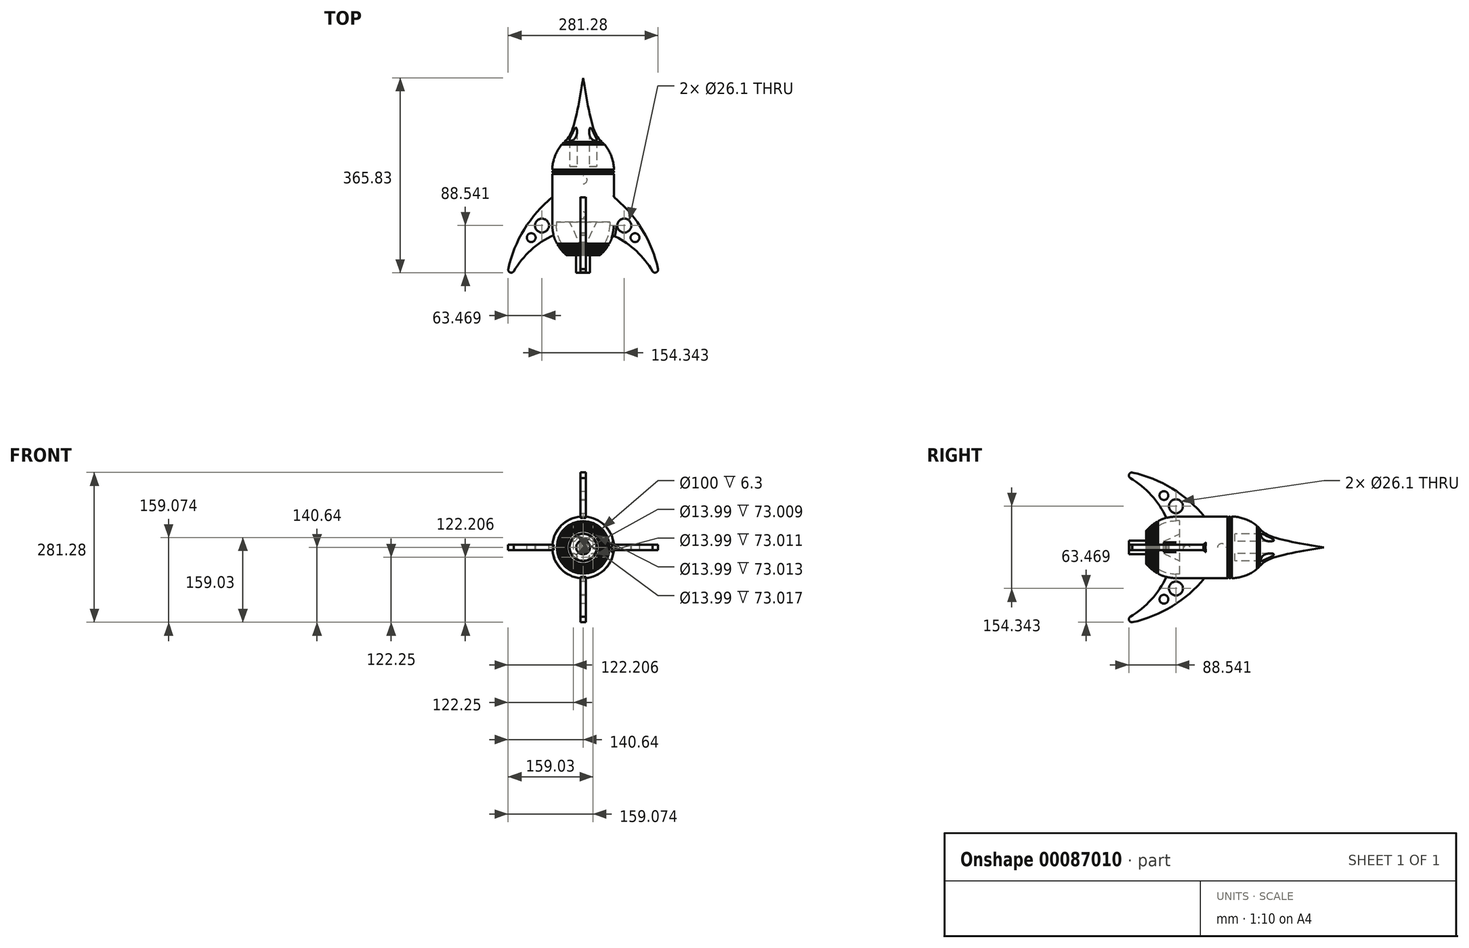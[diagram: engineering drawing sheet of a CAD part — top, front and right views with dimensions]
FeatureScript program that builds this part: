
annotation { "Feature Type Name" : "Feature", "Feature Type Description" : "" }
export const myFeature = defineFeature(function(context is Context, id is Id, definition is map)
    precondition{}
    {
        {
            var Q0;
            Q0=qCreatedBy(makeId("Right.planeOp"),FACE);
            var sketch = newSketch(context, id + "F0", { "sketchPlane" : qUnion([Q0])});
            skLineSegment(sketch, "E0", {"start": v(-55.59, 50) * mm, "end": v(46.96, 50) * mm});
            skArc(sketch, "E1", {"start": v(95.35, 30.1) * mm, "mid": v(73.12, 44.83) * mm, "end": v(46.96, 50) * mm});
            skArc(sketch, "E2", {"start": v(-55.59, 50) * mm, "mid": v(-83.4, 43.72) * mm, "end": v(-105.8, 26.08) * mm});
            skArc(sketch, "E3.0", {"start": v(-55.59, 57.95) * mm, "mid": v(-86.8, 50.89) * mm, "end": v(-111.96, 31.1) * mm});
            skLineSegment(sketch, "E3.1", {"start": v(-55.59, 57.95) * mm, "end": v(46.96, 57.95) * mm});
            skArc(sketch, "E3.2", {"start": v(99.6, 37.03) * mm, "mid": v(75.28, 52.53) * mm, "end": v(46.96, 57.95) * mm});
            skLineSegment(sketch, "E4", {"start": v(-111.96, 31.1) * mm, "end": v(-105.8, 26.08) * mm});
            skLineSegment(sketch, "E5", {"start": v(95.35, 30.1) * mm, "end": v(99.6, 37.03) * mm});
            skLineSegment(sketch, "E6", {"start": v(-312.53, 0) * mm, "end": v(235.17, 0) * mm, "construction": true});
            skLineSegment(sketch, "E7", {"start": v(-103.73, 0) * mm, "end": v(-49.29, 25.17) * mm});
            skLineSegment(sketch, "E8", {"start": v(-49.29, 25.17) * mm, "end": v(-49.29, 50) * mm});
            skLineSegment(sketch, "E9", {"start": v(-49.29, 50) * mm, "end": v(-42.87, 50) * mm});
            skLineSegment(sketch, "E10", {"start": v(-42.87, 50) * mm, "end": v(-42.87, 0) * mm});
            skLineSegment(sketch, "E11", {"start": v(-42.87, 0) * mm, "end": v(-103.73, 0) * mm});
            skFitSpline(sketch, "E12", {"points": [v(99.6, 37.03) * mm, v(116.25, 23.47) * mm, v(221.16, 0) * mm], "startDerivative": vector(38.76, -45.45) * mm, "endDerivative": vector(185.64, -30.52) * mm});
            skLineSegment(sketch, "E13", {"start": v(46.34, 0) * mm, "end": v(221.16, 0) * mm});
            skPoint(sketch, "E14", {"position": v(73.12, 44.83) * mm});
            skLineSegment(sketch, "E15", {"start": v(46.96, 50) * mm, "end": v(48.2, 0) * mm});
            skLineSegment(sketch, "E16", {"start": v(48.2, 0) * mm, "end": v(221.16, 0) * mm});
            skLineSegment(sketch, "E17.bottom", {"start": v(46.96, 50) * mm, "end": v(-42.87, 50) * mm});
            skLineSegment(sketch, "E17.top", {"start": v(46.96, 0) * mm, "end": v(-42.87, 0) * mm});
            skLineSegment(sketch, "E17.left", {"start": v(46.96, 50) * mm, "end": v(46.96, 0) * mm});
            skLineSegment(sketch, "E18", {"start": v(48.2, 0) * mm, "end": v(46.96, 0) * mm});
            skLineSegment(sketch, "E19.bottom", {"start": v(-100.59, 0) * mm, "end": v(-144.67, 0) * mm});
            skLineSegment(sketch, "E19.top", {"start": v(-100.59, 12.97) * mm, "end": v(-144.67, 12.97) * mm});
            skLineSegment(sketch, "E19.left", {"start": v(-100.59, 0) * mm, "end": v(-100.59, 12.97) * mm});
            skLineSegment(sketch, "E19.right", {"start": v(-144.67, 0) * mm, "end": v(-144.67, 12.97) * mm});
            skSolve(sketch);
        }
        {
            var Q0;
            Q0 = qSketchRegion(id + "F0", true);
            var Q1;
            Q1=sQuery(id+"F0.wireOp",EDGE,"E6");
            revolve(context, id + "F1", {"entities" : qUnion([Q0]), "axis" : qUnion([Q1]), "revolveType" : RevolveType.FULL});
        }
        {
            var Q0;
            Q0=qCreatedBy(makeId("Top.planeOp"),FACE);
            var sketch = newSketch(context, id + "F2", { "sketchPlane" : qUnion([Q0])});
            skCircle(sketch, "E20", {"center": v(0, -35.48) * mm, "radius": 5 * mm});
            skCircle(sketch, "E21", {"center": v(0, 29.75) * mm, "radius": 7.5 * mm});
            skSolve(sketch);
        }
        {
            var Q0;
            Q0=makeQuery(id+"F2.imprint","IMPRINT",FACE,{"disambiguationData":[TD([[makeQuery(id+"F2.imprint","IMPRINT",EDGE,{"derivedFrom":sQuery(id+"F2.wireOp",EDGE,"E20")}),1.0]])]});
            extrude(context, id + "F3", {"entities" : qUnion([Q0]), "operationType" : NewBodyOperationType.REMOVE, "endBound" : BoundingType.SYMMETRIC, "depth" : 220.94 * mm});
        }
        {
            var Q0;
            Q0=makeQuery(id+"F2.imprint","IMPRINT",FACE,{"disambiguationData":[TD([[makeQuery(id+"F2.imprint","IMPRINT",EDGE,{"derivedFrom":sQuery(id+"F2.wireOp",EDGE,"E21")}),1.0]])]});
            extrude(context, id + "F4", {"entities" : qUnion([Q0]), "operationType" : NewBodyOperationType.REMOVE, "endBound" : BoundingType.SYMMETRIC, "depth" : 208.68 * mm});
        }
        {
            var Q0;
            Q0=qCreatedBy(makeId("Top.planeOp"),FACE);
            var sketch = newSketch(context, id + "F5", { "sketchPlane" : qUnion([Q0])});
            skArc(sketch, "E22", {"start": v(130.13, -141.96) * mm, "mid": v(97.17, -101.6) * mm, "end": v(53.5, -73.17) * mm});
            skArc(sketch, "E23", {"start": v(140.55, -137.77) * mm, "mid": v(109.33, -61.42) * mm, "end": v(54.26, 0) * mm});
            skLineSegment(sketch, "E24", {"start": v(53.5, -73.17) * mm, "end": v(54.26, 0) * mm});
            skArc(sketch, "E25", {"start": v(130.13, -141.96) * mm, "mid": v(137.28, -143.98) * mm, "end": v(140.44, -137.26) * mm});
            skCircle(sketch, "E26", {"center": v(77.17, -56.13) * mm, "radius": 13.05 * mm});
            skCircle(sketch, "E27", {"center": v(97.37, -78.71) * mm, "radius": 8.3 * mm});
            skSolve(sketch);
        }
        {
            var Q0;
            Q0=makeQuery(id+"F5.imprint","IMPRINT",FACE,{"disambiguationData":[TD([[makeQuery(id+"F5.imprint","IMPRINT",EDGE,{"derivedFrom":sQuery(id+"F5.wireOp",EDGE,"E22")}),-1.0]])]});
            extrude(context, id + "F6", {"entities" : qUnion([Q0]), "operationType" : NewBodyOperationType.ADD, "endBound" : BoundingType.SYMMETRIC, "depth" : 10 * mm});
        }
        {
            var Q0;
            Q0=makeQuery(id+"F1.opRevolve","SWEPT_BODY",BODY,{"disambiguationData":[OSD([sQuery(id+"F0.wireOp",EDGE,"E0"),sQuery(id+"F0.wireOp",EDGE,"E1"),sQuery(id+"F0.wireOp",EDGE,"E2"),sQuery(id+"F0.wireOp",EDGE,"E3.0"),sQuery(id+"F0.wireOp",EDGE,"E3.1"),sQuery(id+"F0.wireOp",EDGE,"E3.2"),sQuery(id+"F0.wireOp",EDGE,"E4"),sQuery(id+"F0.wireOp",EDGE,"E5")])]});
            var Q1;
            Q1=sQuery(id+"F0.wireOp",EDGE,"E6");
            circularPattern(context, id + "F7", {"operationType" : NewBodyOperationType.ADD, "entities" : qUnion([Q0]), "axis" : qUnion([Q1]), "angle" : 360 * degree, "instanceCount" : 4, "equalSpace" : true});
        }
        {
            var Q0;
            Q0=qCreatedBy(makeId("Front.planeOp"),FACE);
            var sketch = newSketch(context, id + "F8", { "sketchPlane" : qUnion([Q0])});
            skCircle(sketch, "E28", {"center": v(-18.4, -18.43) * mm, "radius": 7 * mm});
            skCircle(sketch, "E29.1.0", {"center": v(18.43, -18.4) * mm, "radius": 7 * mm});
            skCircle(sketch, "E29.2.0", {"center": v(18.4, 18.43) * mm, "radius": 7 * mm});
            skCircle(sketch, "E29.3.0", {"center": v(-18.43, 18.4) * mm, "radius": 7 * mm});
            skPoint(sketch, "E29.center", {"position": v(0, 0) * mm});
            skSolve(sketch);
        }
        {
            var Q0;
            Q0=makeQuery(id+"F8.imprint","IMPRINT",FACE,{"disambiguationData":[TD([[makeQuery(id+"F8.imprint","IMPRINT",EDGE,{"derivedFrom":sQuery(id+"F8.wireOp",EDGE,"E28")}),1.0]])]});
            var Q1;
            Q1=makeQuery(id+"F8.imprint","IMPRINT",FACE,{"disambiguationData":[TD([[makeQuery(id+"F8.imprint","IMPRINT",EDGE,{"derivedFrom":sQuery(id+"F8.wireOp",EDGE,"E29.3.0")}),1.0]])]});
            var Q2;
            Q2=makeQuery(id+"F8.imprint","IMPRINT",FACE,{"disambiguationData":[TD([[makeQuery(id+"F8.imprint","IMPRINT",EDGE,{"derivedFrom":sQuery(id+"F8.wireOp",EDGE,"E29.2.0")}),1.0]])]});
            var Q3;
            Q3=makeQuery(id+"F8.imprint","IMPRINT",FACE,{"disambiguationData":[TD([[makeQuery(id+"F8.imprint","IMPRINT",EDGE,{"derivedFrom":sQuery(id+"F8.wireOp",EDGE,"E29.1.0")}),1.0]])]});
            extrude(context, id + "F9", {"entities" : qUnion([Q0, Q1, Q2, Q3]), "oppositeDirection" : true, "depth" : 171.7 * mm, "hasSecondDirection" : true, "secondDirectionOppositeDirection" : true, "secondDirectionDepth" : 54.52 * mm});
        }
        {
            var Q0;
            Q0=makeQuery(id+"F9.opExtrude","SWEPT_BODY",BODY,{"disambiguationData":[OSD([sQuery(id+"F8.wireOp",EDGE,"E29.3.0")])]});
            var Q1;
            Q1=makeQuery(id+"F9.opExtrude","SWEPT_BODY",BODY,{"disambiguationData":[OSD([sQuery(id+"F8.wireOp",EDGE,"E29.2.0")])]});
            var Q2;
            Q2=makeQuery(id+"F9.opExtrude","SWEPT_BODY",BODY,{"disambiguationData":[OSD([sQuery(id+"F8.wireOp",EDGE,"E29.1.0")])]});
            var Q3;
            Q3=makeQuery(id+"F9.opExtrude","SWEPT_BODY",BODY,{"disambiguationData":[OSD([sQuery(id+"F8.wireOp",EDGE,"E28")])]});
            var Q4;
            Q4=makeQuery(id+"F1.opRevolve","SWEPT_BODY",BODY,{"disambiguationData":[OSD([sQuery(id+"F0.wireOp",EDGE,"E0"),sQuery(id+"F0.wireOp",EDGE,"E1"),sQuery(id+"F0.wireOp",EDGE,"E2"),sQuery(id+"F0.wireOp",EDGE,"E3.0"),sQuery(id+"F0.wireOp",EDGE,"E3.1"),sQuery(id+"F0.wireOp",EDGE,"E3.2"),sQuery(id+"F0.wireOp",EDGE,"E4"),sQuery(id+"F0.wireOp",EDGE,"E7"),sQuery(id+"F0.wireOp",EDGE,"E8"),sQuery(id+"F0.wireOp",EDGE,"E10"),sQuery(id+"F0.wireOp",EDGE,"E11"),sQuery(id+"F0.wireOp",EDGE,"E12"),sQuery(id+"F0.wireOp",EDGE,"8e6c7944-2847-4c8e-8d39-0e6d0a6cfa01"),sQuery(id+"F0.wireOp",EDGE,"E13")])]});
            booleanBodies(context, id + "F10", {"operationType" : BooleanOperationType.SUBTRACTION, "tools" : qUnion([Q0, Q1, Q2, Q3]), "targets" : qUnion([Q4])});
        }
        {
            var Q0;
            Q0=makeQuery(id+"F7.opPattern","COPY",EDGE,{"derivedFrom":makeQuery(id+"F6.boolean.opBoolean","INTERSECT",EDGE,{"derivedFrom":[makeQuery(id+"F1.opRevolve","SWEPT_FACE",FACE,{"disambiguationData":[OSD([sQuery(id+"F0.wireOp",EDGE,"E3.1")])]}),makeQuery(id+"F6.opExtrude","CAP_FACE",FACE,{"disambiguationData":[OSD([sQuery(id+"F5.wireOp",EDGE,"E22"),sQuery(id+"F5.wireOp",EDGE,"E23"),sQuery(id+"F5.wireOp",EDGE,"E24")])],"isStart":false})]}),"instanceName":"1"});
            var Q1;
            Q1=makeQuery(id+"F7.opPattern","COPY",EDGE,{"derivedFrom":makeQuery(id+"F6.boolean.opBoolean","INTERSECT",EDGE,{"derivedFrom":[makeQuery(id+"F1.opRevolve","SWEPT_FACE",FACE,{"disambiguationData":[OSD([sQuery(id+"F0.wireOp",EDGE,"E3.0")])]}),makeQuery(id+"F6.opExtrude","CAP_FACE",FACE,{"disambiguationData":[OSD([sQuery(id+"F5.wireOp",EDGE,"E22"),sQuery(id+"F5.wireOp",EDGE,"E23"),sQuery(id+"F5.wireOp",EDGE,"E24")])],"isStart":false})]}),"instanceName":"1"});
            var Q2;
            Q2=makeQuery(id+"F6.boolean.opBoolean","INTERSECT",EDGE,{"derivedFrom":[makeQuery(id+"F1.opRevolve","SWEPT_FACE",FACE,{"disambiguationData":[OSD([sQuery(id+"F0.wireOp",EDGE,"E3.0")])]}),makeQuery(id+"F6.opExtrude","CAP_FACE",FACE,{"disambiguationData":[OSD([sQuery(id+"F5.wireOp",EDGE,"E22"),sQuery(id+"F5.wireOp",EDGE,"E23"),sQuery(id+"F5.wireOp",EDGE,"E24")])],"isStart":true})]});
            var Q3;
            Q3=makeQuery(id+"F6.boolean.opBoolean","INTERSECT",EDGE,{"derivedFrom":[makeQuery(id+"F1.opRevolve","SWEPT_FACE",FACE,{"disambiguationData":[OSD([sQuery(id+"F0.wireOp",EDGE,"E3.1")])]}),makeQuery(id+"F6.opExtrude","CAP_FACE",FACE,{"disambiguationData":[OSD([sQuery(id+"F5.wireOp",EDGE,"E22"),sQuery(id+"F5.wireOp",EDGE,"E23"),sQuery(id+"F5.wireOp",EDGE,"E24")])],"isStart":true})]});
            var Q4;
            Q4=makeQuery(id+"F7.opPattern","COPY",EDGE,{"derivedFrom":makeQuery(id+"F6.boolean.opBoolean","INTERSECT",EDGE,{"derivedFrom":[makeQuery(id+"F1.opRevolve","SWEPT_FACE",FACE,{"disambiguationData":[OSD([sQuery(id+"F0.wireOp",EDGE,"E3.1")])]}),makeQuery(id+"F6.opExtrude","CAP_FACE",FACE,{"disambiguationData":[OSD([sQuery(id+"F5.wireOp",EDGE,"E22"),sQuery(id+"F5.wireOp",EDGE,"E23"),sQuery(id+"F5.wireOp",EDGE,"E24")])],"isStart":true})]}),"instanceName":"1"});
            var Q5;
            {var subQ0=makeQuery(id+"F1.opRevolve","SWEPT_FACE",FACE,{"disambiguationData":[OSD([sQuery(id+"F0.wireOp",EDGE,"E3.1")])]});Q5=makeQuery(id+"F7.boolean.opBoolean","INTERSECT",EDGE,{"disambiguationData":[OD(1.0)],"derivedFrom":[makeQuery(id+"F7.opPattern","COPY",FACE,{"derivedFrom":subQ0,"instanceName":"1"}),makeQuery(id+"F7.opPattern","COPY",FACE,{"derivedFrom":subQ0,"instanceName":"2"}),makeQuery(id+"F7.opPattern","COPY",FACE,{"derivedFrom":subQ0,"instanceName":"3"})]});}
            var Q6;
            Q6=makeQuery(id+"F6.boolean.opBoolean","INTERSECT",EDGE,{"derivedFrom":[makeQuery(id+"F1.opRevolve","SWEPT_FACE",FACE,{"disambiguationData":[OSD([sQuery(id+"F0.wireOp",EDGE,"E3.1")])]}),makeQuery(id+"F6.opExtrude","CAP_FACE",FACE,{"disambiguationData":[OSD([sQuery(id+"F5.wireOp",EDGE,"E22"),sQuery(id+"F5.wireOp",EDGE,"E23"),sQuery(id+"F5.wireOp",EDGE,"E24")])],"isStart":false})]});
            var Q7;
            {var subQ0=makeQuery(id+"F1.opRevolve","SWEPT_FACE",FACE,{"disambiguationData":[OSD([sQuery(id+"F0.wireOp",EDGE,"E3.1")])]});Q7=makeQuery(id+"F7.boolean.opBoolean","INTERSECT",EDGE,{"disambiguationData":[OD(3.0)],"derivedFrom":[makeQuery(id+"F7.opPattern","COPY",FACE,{"derivedFrom":subQ0,"instanceName":"1"}),makeQuery(id+"F7.opPattern","COPY",FACE,{"derivedFrom":subQ0,"instanceName":"2"}),makeQuery(id+"F7.opPattern","COPY",FACE,{"derivedFrom":subQ0,"instanceName":"3"})]});}
            var Q8;
            {var subQ0=makeQuery(id+"F1.opRevolve","SWEPT_FACE",FACE,{"disambiguationData":[OSD([sQuery(id+"F0.wireOp",EDGE,"E3.1")])]});Q8=makeQuery(id+"F7.boolean.opBoolean","INTERSECT",EDGE,{"disambiguationData":[OD(0.0)],"derivedFrom":[makeQuery(id+"F7.opPattern","COPY",FACE,{"derivedFrom":subQ0,"instanceName":"1"}),makeQuery(id+"F7.opPattern","COPY",FACE,{"derivedFrom":subQ0,"instanceName":"2"}),makeQuery(id+"F7.opPattern","COPY",FACE,{"derivedFrom":subQ0,"instanceName":"3"})]});}
            var Q9;
            {var subQ0=makeQuery(id+"F1.opRevolve","SWEPT_FACE",FACE,{"disambiguationData":[OSD([sQuery(id+"F0.wireOp",EDGE,"E3.0")])]});Q9=makeQuery(id+"F7.boolean.opBoolean","INTERSECT",EDGE,{"disambiguationData":[OD(0.0)],"derivedFrom":[makeQuery(id+"F7.opPattern","COPY",FACE,{"derivedFrom":subQ0,"instanceName":"1"}),makeQuery(id+"F7.opPattern","COPY",FACE,{"derivedFrom":subQ0,"instanceName":"3"})]});}
            var Q10;
            {var subQ0=makeQuery(id+"F1.opRevolve","SWEPT_FACE",FACE,{"disambiguationData":[OSD([sQuery(id+"F0.wireOp",EDGE,"E3.0")])]});Q10=makeQuery(id+"F7.boolean.opBoolean","INTERSECT",EDGE,{"disambiguationData":[OD(0.0)],"derivedFrom":[makeQuery(id+"F7.opPattern","COPY",FACE,{"derivedFrom":subQ0,"instanceName":"1"}),makeQuery(id+"F7.opPattern","COPY",FACE,{"derivedFrom":subQ0,"instanceName":"2"})]});}
            var Q11;
            {var subQ0=makeQuery(id+"F1.opRevolve","SWEPT_FACE",FACE,{"disambiguationData":[OSD([sQuery(id+"F0.wireOp",EDGE,"E3.1")])]});Q11=makeQuery(id+"F7.boolean.opBoolean","INTERSECT",EDGE,{"disambiguationData":[OD(4.0)],"derivedFrom":[makeQuery(id+"F7.opPattern","COPY",FACE,{"derivedFrom":subQ0,"instanceName":"1"}),makeQuery(id+"F7.opPattern","COPY",FACE,{"derivedFrom":subQ0,"instanceName":"2"}),makeQuery(id+"F7.opPattern","COPY",FACE,{"derivedFrom":subQ0,"instanceName":"3"})]});}
            var Q12;
            Q12=makeQuery(id+"F6.boolean.opBoolean","INTERSECT",EDGE,{"derivedFrom":[makeQuery(id+"F1.opRevolve","SWEPT_FACE",FACE,{"disambiguationData":[OSD([sQuery(id+"F0.wireOp",EDGE,"E3.0")])]}),makeQuery(id+"F6.opExtrude","SWEPT_FACE",FACE,{"disambiguationData":[OSD([sQuery(id+"F5.wireOp",EDGE,"E22")])]})]});
            var Q13;
            Q13=makeQuery(id+"F7.opPattern","COPY",EDGE,{"derivedFrom":makeQuery(id+"F6.boolean.opBoolean","INTERSECT",EDGE,{"derivedFrom":[makeQuery(id+"F1.opRevolve","SWEPT_FACE",FACE,{"disambiguationData":[OSD([sQuery(id+"F0.wireOp",EDGE,"E3.0")])]}),makeQuery(id+"F6.opExtrude","SWEPT_FACE",FACE,{"disambiguationData":[OSD([sQuery(id+"F5.wireOp",EDGE,"E22")])]})]}),"instanceName":"1"});
            var Q14;
            Q14=makeQuery(id+"F7.opPattern","COPY",EDGE,{"derivedFrom":makeQuery(id+"F6.boolean.opBoolean","INTERSECT",EDGE,{"derivedFrom":[makeQuery(id+"F1.opRevolve","SWEPT_FACE",FACE,{"disambiguationData":[OSD([sQuery(id+"F0.wireOp",EDGE,"E3.1")])]}),makeQuery(id+"F6.opExtrude","SWEPT_FACE",FACE,{"disambiguationData":[OSD([sQuery(id+"F5.wireOp",EDGE,"E23")])]})]}),"instanceName":"1"});
            var Q15;
            Q15=makeQuery(id+"F6.boolean.opBoolean","INTERSECT",EDGE,{"derivedFrom":[makeQuery(id+"F1.opRevolve","SWEPT_FACE",FACE,{"disambiguationData":[OSD([sQuery(id+"F0.wireOp",EDGE,"E3.1")])]}),makeQuery(id+"F6.opExtrude","SWEPT_FACE",FACE,{"disambiguationData":[OSD([sQuery(id+"F5.wireOp",EDGE,"E23")])]})]});
            var Q16;
            {var subQ0=makeQuery(id+"F1.opRevolve","SWEPT_FACE",FACE,{"disambiguationData":[OSD([sQuery(id+"F0.wireOp",EDGE,"E3.1")])]});Q16=makeQuery(id+"F7.boolean.opBoolean","INTERSECT",EDGE,{"disambiguationData":[OD(2.0)],"derivedFrom":[makeQuery(id+"F7.opPattern","COPY",FACE,{"derivedFrom":subQ0,"instanceName":"1"}),makeQuery(id+"F7.opPattern","COPY",FACE,{"derivedFrom":subQ0,"instanceName":"2"}),makeQuery(id+"F7.opPattern","COPY",FACE,{"derivedFrom":subQ0,"instanceName":"3"})]});}
            var Q17;
            {var subQ0=makeQuery(id+"F1.opRevolve","SWEPT_FACE",FACE,{"disambiguationData":[OSD([sQuery(id+"F0.wireOp",EDGE,"E3.1")])]});Q17=makeQuery(id+"F7.boolean.opBoolean","INTERSECT",EDGE,{"disambiguationData":[OD(5.0)],"derivedFrom":[makeQuery(id+"F7.opPattern","COPY",FACE,{"derivedFrom":subQ0,"instanceName":"1"}),makeQuery(id+"F7.opPattern","COPY",FACE,{"derivedFrom":subQ0,"instanceName":"2"}),makeQuery(id+"F7.opPattern","COPY",FACE,{"derivedFrom":subQ0,"instanceName":"3"})]});}
            fillet(context, id + "F11", {"entities" : qUnion([Q0, Q1, Q2, Q3, Q4, Q5, Q6, Q7, Q8, Q9, Q10, Q11, Q12, Q13, Q14, Q15, Q16, Q17]), "radius" : 5 * mm, "tangentPropagation" : true, "allowEdgeOverflow" : false});
        }
        {
            var Q0;
            Q0=qCreatedBy(makeId("Top.planeOp"),FACE);
            var sketch = newSketch(context, id + "F12", { "sketchPlane" : qUnion([Q0])});
            skCircle(sketch, "E30.cCircle", {"center": v(-39.96, 97.08) * mm, "radius": 1.5 * mm, "construction": true});
            skLineSegment(sketch, "E30.0", {"start": v(-39.36, 95.45) * mm, "end": v(-41.07, 95.75) * mm});
            skLineSegment(sketch, "E30.1", {"start": v(-41.07, 95.75) * mm, "end": v(-41.67, 97.37) * mm});
            skLineSegment(sketch, "E30.2", {"start": v(-41.67, 97.37) * mm, "end": v(-40.56, 98.7) * mm});
            skLineSegment(sketch, "E30.3", {"start": v(-40.56, 98.7) * mm, "end": v(-38.85, 98.4) * mm});
            skLineSegment(sketch, "E30.4", {"start": v(-38.85, 98.4) * mm, "end": v(-38.25, 96.78) * mm});
            skLineSegment(sketch, "E30.5", {"start": v(-38.25, 96.78) * mm, "end": v(-39.36, 95.45) * mm});
            skPoint(sketch, "E30.0.midPoint", {"position": v(-40.21, 95.6) * mm});
            skCircle(sketch, "E31.cCircle", {"center": v(-36.5, 100.73) * mm, "radius": 1.5 * mm, "construction": true});
            skLineSegment(sketch, "E31.0", {"start": v(-34.83, 100.25) * mm, "end": v(-36.09, 99.05) * mm});
            skLineSegment(sketch, "E31.1", {"start": v(-36.09, 99.05) * mm, "end": v(-37.75, 99.54) * mm});
            skLineSegment(sketch, "E31.2", {"start": v(-37.75, 99.54) * mm, "end": v(-38.16, 101.22) * mm});
            skLineSegment(sketch, "E31.3", {"start": v(-38.16, 101.22) * mm, "end": v(-36.9, 102.42) * mm});
            skLineSegment(sketch, "E31.4", {"start": v(-36.9, 102.42) * mm, "end": v(-35.25, 101.93) * mm});
            skLineSegment(sketch, "E31.5", {"start": v(-35.25, 101.93) * mm, "end": v(-34.83, 100.25) * mm});
            skPoint(sketch, "E31.0.midPoint", {"position": v(-35.46, 99.65) * mm});
            skCircle(sketch, "E32.cCircle", {"center": v(-58.26, 42.27) * mm, "radius": 1.5 * mm, "construction": true});
            skLineSegment(sketch, "E32.0", {"start": v(-58.29, 40.54) * mm, "end": v(-59.77, 41.43) * mm});
            skLineSegment(sketch, "E32.1", {"start": v(-59.77, 41.43) * mm, "end": v(-59.74, 43.16) * mm});
            skLineSegment(sketch, "E32.2", {"start": v(-59.74, 43.16) * mm, "end": v(-58.23, 44) * mm});
            skLineSegment(sketch, "E32.3", {"start": v(-58.23, 44) * mm, "end": v(-56.74, 43.11) * mm});
            skLineSegment(sketch, "E32.4", {"start": v(-56.74, 43.11) * mm, "end": v(-56.77, 41.38) * mm});
            skLineSegment(sketch, "E32.5", {"start": v(-56.77, 41.38) * mm, "end": v(-58.29, 40.54) * mm});
            skPoint(sketch, "E32.0.midPoint", {"position": v(-59.03, 40.99) * mm});
            skCircle(sketch, "E33.cCircle", {"center": v(-58.21, 47.36) * mm, "radius": 1.5 * mm, "construction": true});
            skLineSegment(sketch, "E33.0", {"start": v(-56.73, 46.47) * mm, "end": v(-58.24, 45.63) * mm});
            skLineSegment(sketch, "E33.1", {"start": v(-58.24, 45.63) * mm, "end": v(-59.73, 46.51) * mm});
            skLineSegment(sketch, "E33.2", {"start": v(-59.73, 46.51) * mm, "end": v(-59.7, 48.25) * mm});
            skLineSegment(sketch, "E33.3", {"start": v(-59.7, 48.25) * mm, "end": v(-58.19, 49.1) * mm});
            skLineSegment(sketch, "E33.4", {"start": v(-58.19, 49.1) * mm, "end": v(-56.7, 48.2) * mm});
            skLineSegment(sketch, "E33.5", {"start": v(-56.7, 48.2) * mm, "end": v(-56.73, 46.47) * mm});
            skPoint(sketch, "E33.0.midPoint", {"position": v(-57.48, 46.05) * mm});
            skCircle(sketch, "E34.cCircle", {"center": v(-36.17, -107.7) * mm, "radius": 1.5 * mm, "construction": true});
            skLineSegment(sketch, "E34.0", {"start": v(-36.57, -109.39) * mm, "end": v(-37.83, -108.2) * mm});
            skLineSegment(sketch, "E34.1", {"start": v(-37.83, -108.2) * mm, "end": v(-37.42, -106.51) * mm});
            skLineSegment(sketch, "E34.2", {"start": v(-37.42, -106.51) * mm, "end": v(-35.76, -106.02) * mm});
            skLineSegment(sketch, "E34.3", {"start": v(-35.76, -106.02) * mm, "end": v(-34.5, -107.21) * mm});
            skLineSegment(sketch, "E34.4", {"start": v(-34.5, -107.21) * mm, "end": v(-34.9, -108.9) * mm});
            skLineSegment(sketch, "E34.5", {"start": v(-34.9, -108.9) * mm, "end": v(-36.57, -109.39) * mm});
            skPoint(sketch, "E34.0.midPoint", {"position": v(-37.2, -108.8) * mm});
            skCircle(sketch, "E35.cCircle", {"center": v(-39.75, -103.95) * mm, "radius": 1.5 * mm, "construction": true});
            skLineSegment(sketch, "E35.0", {"start": v(-38.05, -103.6) * mm, "end": v(-38.6, -105.25) * mm});
            skLineSegment(sketch, "E35.1", {"start": v(-38.6, -105.25) * mm, "end": v(-40.3, -105.59) * mm});
            skLineSegment(sketch, "E35.2", {"start": v(-40.3, -105.59) * mm, "end": v(-41.45, -104.29) * mm});
            skLineSegment(sketch, "E35.3", {"start": v(-41.45, -104.29) * mm, "end": v(-40.9, -102.65) * mm});
            skLineSegment(sketch, "E35.4", {"start": v(-40.9, -102.65) * mm, "end": v(-39.2, -102.3) * mm});
            skLineSegment(sketch, "E35.5", {"start": v(-39.2, -102.3) * mm, "end": v(-38.05, -103.6) * mm});
            skPoint(sketch, "E35.0.midPoint", {"position": v(-38.33, -104.43) * mm});
            skLineSegment(sketch, "E36", {"start": v(-37.42, -106.51) * mm, "end": v(-38.6, -105.25) * mm});
            skCircle(sketch, "E37.cCircle", {"center": v(-43.11, -99.99) * mm, "radius": 1.5 * mm, "construction": true});
            skLineSegment(sketch, "E37.0", {"start": v(-41.4, -99.72) * mm, "end": v(-42.03, -101.34) * mm});
            skLineSegment(sketch, "E37.1", {"start": v(-42.03, -101.34) * mm, "end": v(-43.74, -101.6) * mm});
            skLineSegment(sketch, "E37.2", {"start": v(-43.74, -101.6) * mm, "end": v(-44.83, -100.26) * mm});
            skLineSegment(sketch, "E37.3", {"start": v(-44.83, -100.26) * mm, "end": v(-44.2, -98.64) * mm});
            skLineSegment(sketch, "E37.4", {"start": v(-44.2, -98.64) * mm, "end": v(-42.5, -98.37) * mm});
            skLineSegment(sketch, "E37.5", {"start": v(-42.5, -98.37) * mm, "end": v(-41.4, -99.72) * mm});
            skPoint(sketch, "E37.0.midPoint", {"position": v(-41.71, -100.53) * mm});
            skLineSegment(sketch, "E38", {"start": v(-40.9, -102.65) * mm, "end": v(-42.03, -101.34) * mm});
            skCircle(sketch, "E39.cCircle", {"center": v(-46.17, -95.8) * mm, "radius": 1.5 * mm, "construction": true});
            skLineSegment(sketch, "E39.0", {"start": v(-44.44, -95.75) * mm, "end": v(-45.26, -97.27) * mm});
            skLineSegment(sketch, "E39.1", {"start": v(-45.26, -97.27) * mm, "end": v(-47, -97.32) * mm});
            skLineSegment(sketch, "E39.2", {"start": v(-47, -97.32) * mm, "end": v(-47.9, -95.85) * mm});
            skLineSegment(sketch, "E39.3", {"start": v(-47.9, -95.85) * mm, "end": v(-47.08, -94.32) * mm});
            skLineSegment(sketch, "E39.4", {"start": v(-47.08, -94.32) * mm, "end": v(-45.35, -94.27) * mm});
            skLineSegment(sketch, "E39.5", {"start": v(-45.35, -94.27) * mm, "end": v(-44.44, -95.75) * mm});
            skPoint(sketch, "E39.0.midPoint", {"position": v(-44.85, -96.51) * mm});
            skLineSegment(sketch, "E40", {"start": v(-44.2, -98.64) * mm, "end": v(-45.26, -97.27) * mm});
            skCircle(sketch, "E41.cCircle", {"center": v(-48.82, -91.34) * mm, "radius": 1.5 * mm, "construction": true});
            skLineSegment(sketch, "E41.0", {"start": v(-47.1, -91.49) * mm, "end": v(-48.08, -92.91) * mm});
            skLineSegment(sketch, "E41.1", {"start": v(-48.08, -92.91) * mm, "end": v(-49.8, -92.77) * mm});
            skLineSegment(sketch, "E41.2", {"start": v(-49.8, -92.77) * mm, "end": v(-50.55, -91.2) * mm});
            skLineSegment(sketch, "E41.3", {"start": v(-50.55, -91.2) * mm, "end": v(-49.56, -89.78) * mm});
            skLineSegment(sketch, "E41.4", {"start": v(-49.56, -89.78) * mm, "end": v(-47.83, -89.92) * mm});
            skLineSegment(sketch, "E41.5", {"start": v(-47.83, -89.92) * mm, "end": v(-47.1, -91.49) * mm});
            skPoint(sketch, "E41.0.midPoint", {"position": v(-47.59, -92.2) * mm});
            skLineSegment(sketch, "E42", {"start": v(-47.08, -94.32) * mm, "end": v(-48.08, -92.91) * mm});
            skSolve(sketch);
        }
        {
            var Q0;
            Q0 = qSketchRegion(id + "F12", true);
            var Q1;
            Q1=sQuery(id+"F0.wireOp",EDGE,"E6");
            revolve(context, id + "F13", {"operationType" : NewBodyOperationType.REMOVE, "entities" : qUnion([Q0]), "axis" : qUnion([Q1]), "revolveType" : RevolveType.FULL, "oppositeDirection" : true});
        }
    });
